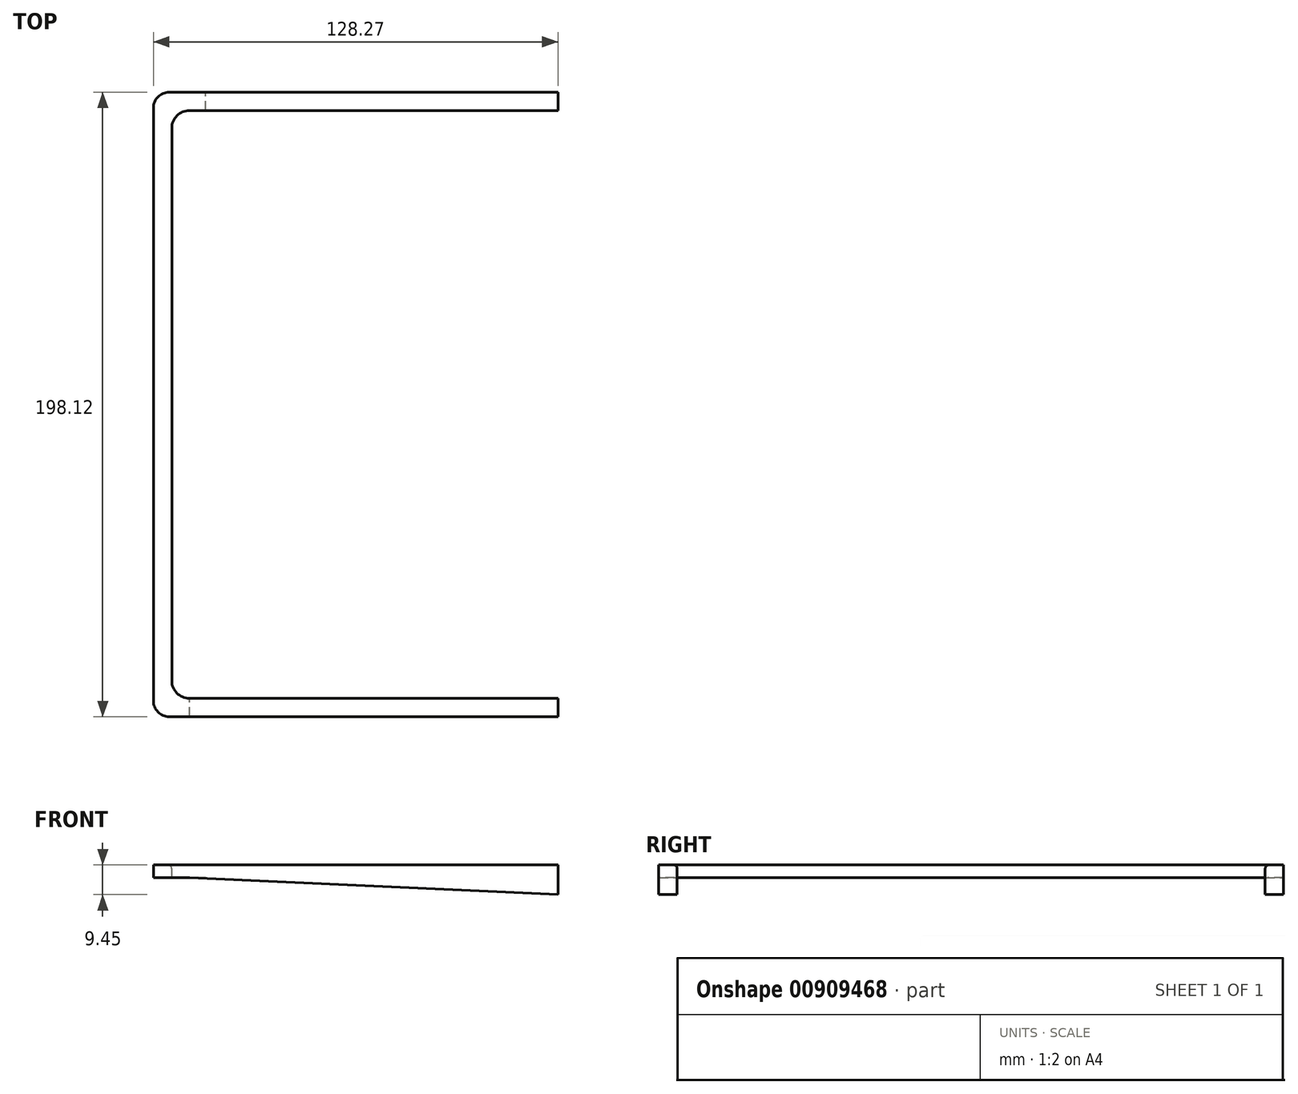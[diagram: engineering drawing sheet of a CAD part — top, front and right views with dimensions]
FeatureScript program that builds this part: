
annotation { "Feature Type Name" : "Feature", "Feature Type Description" : "" }
export const myFeature = defineFeature(function(context is Context, id is Id, definition is map)
    precondition{}
    {
        {
            var Q0;
            Q0=qCreatedBy(makeId("Top.planeOp"),FACE);
            var sketch = newSketch(context, id + "F0", { "sketchPlane" : qUnion([Q0])});
            skLineSegment(sketch, "E0", {"start": v(82.03, -99.06) * mm, "end": v(-41.16, -99.06) * mm});
            skArc(sketch, "E1", {"start": v(-46.24, -93.98) * mm, "mid": v(-44.75, -97.57) * mm, "end": v(-41.16, -99.06) * mm});
            skLineSegment(sketch, "E2", {"start": v(-46.24, -93.98) * mm, "end": v(-46.24, 93.98) * mm});
            skLineSegment(sketch, "E3", {"start": v(-41.16, 99.06) * mm, "end": v(82.03, 99.06) * mm});
            skArc(sketch, "E4", {"start": v(-41.16, 99.06) * mm, "mid": v(-44.75, 97.57) * mm, "end": v(-46.24, 93.98) * mm});
            skLineSegment(sketch, "E5", {"start": v(82.03, 93.22) * mm, "end": v(-34.8, 93.22) * mm});
            skArc(sketch, "E6", {"start": v(-34.8, 93.22) * mm, "mid": v(-38.76, 91.58) * mm, "end": v(-40.4, 87.63) * mm});
            skLineSegment(sketch, "E7", {"start": v(-40.4, 87.63) * mm, "end": v(-40.4, -87.63) * mm});
            skArc(sketch, "E8", {"start": v(-40.4, -87.63) * mm, "mid": v(-38.76, -91.58) * mm, "end": v(-34.8, -93.22) * mm});
            skLineSegment(sketch, "E9", {"start": v(-34.8, -93.22) * mm, "end": v(82.03, -93.22) * mm});
            skLineSegment(sketch, "E10", {"start": v(82.03, 99.06) * mm, "end": v(82.03, 93.22) * mm});
            skLineSegment(sketch, "E11", {"start": v(82.03, -93.22) * mm, "end": v(82.03, -99.06) * mm});
            skSolve(sketch);
        }
        {
            var Q0;
            Q0 = qSketchRegion(id + "F0", true);
            extrude(context, id + "F1", {"entities" : qUnion([Q0]), "oppositeDirection" : true, "depth" : 4.06 * mm, "offsetDistance" : 25.4 * mm});
        }
        {
            var Q0;
            Q0=makeQuery(id+"F1.opExtrude","CAP_FACE",FACE,{"disambiguationData":[OSD([sQuery(id+"F0.wireOp",EDGE,"E0"),sQuery(id+"F0.wireOp",EDGE,"E1"),sQuery(id+"F0.wireOp",EDGE,"E2"),sQuery(id+"F0.wireOp",EDGE,"E3"),sQuery(id+"F0.wireOp",EDGE,"E4"),sQuery(id+"F0.wireOp",EDGE,"E5"),sQuery(id+"F0.wireOp",EDGE,"E6"),sQuery(id+"F0.wireOp",EDGE,"E7"),sQuery(id+"F0.wireOp",EDGE,"E8"),sQuery(id+"F0.wireOp",EDGE,"E9"),sQuery(id+"F0.wireOp",EDGE,"E10"),sQuery(id+"F0.wireOp",EDGE,"E11")])],"isStart":true});
            var sketch = newSketch(context, id + "F2", { "sketchPlane" : qUnion([Q0])});
            skLineSegment(sketch, "E12", {"start": v(-34.8, 93.22) * mm, "end": v(-34.8, 99.06) * mm});
            skSolve(sketch);
        }
        {
            var Q0;
            Q0=makeQuery(id+"F1.opExtrude","SWEPT_FACE",FACE,{"disambiguationData":[OSD([sQuery(id+"F0.wireOp",EDGE,"E3")])]});
            var sketch = newSketch(context, id + "F3", { "sketchPlane" : qUnion([Q0])});
            skLineSegment(sketch, "E13", {"start": v(-82.03, 0) * mm, "end": v(-82.03, -9.45) * mm});
            skLineSegment(sketch, "E14", {"start": v(-82.03, -9.45) * mm, "end": v(35, -3.8) * mm});
            skLineSegment(sketch, "E15", {"start": v(35, -3.8) * mm, "end": v(34.8, 0) * mm});
            skSolve(sketch);
        }
        {
            var Q0;
            {var subQ0=sQuery(id+"F3.wireOp",EDGE,"E13");Q0=makeQuery(id+"F3.imprint","IMPRINT",FACE,{"disambiguationData":[TD([[makeQuery(id+"F3.imprint","IMPRINT",EDGE,{"derivedFrom":subQ0}),1.0]])]});}
            var Q1;
            Q1=makeQuery(id+"F1.opExtrude","SWEPT_FACE",FACE,{"disambiguationData":[OSD([sQuery(id+"F0.wireOp",EDGE,"E5")])]});
            extrude(context, id + "F4", {"entities" : qUnion([Q0]), "operationType" : NewBodyOperationType.ADD, "endBound" : BoundingType.UP_TO_SURFACE, "oppositeDirection" : true, "depth" : 25.4 * mm, "endBoundEntityFace" : qUnion([Q1]), "offsetDistance" : 25.4 * mm});
        }
        {
            var Q0;
            Q0=makeQuery(id+"F1.opExtrude","SWEPT_FACE",FACE,{"disambiguationData":[OSD([sQuery(id+"F0.wireOp",EDGE,"E9")])]});
            var sketch = newSketch(context, id + "F5", { "sketchPlane" : qUnion([Q0])});
            skLineSegment(sketch, "E16", {"start": v(-82.03, 0) * mm, "end": v(-82.03, -9.45) * mm});
            skLineSegment(sketch, "E17", {"start": v(-82.03, -9.45) * mm, "end": v(34.8, -4.06) * mm});
            skLineSegment(sketch, "E18", {"start": v(34.8, -4.06) * mm, "end": v(34.8, 0) * mm});
            skLineSegment(sketch, "E19", {"start": v(34.8, 0) * mm, "end": v(-82.03, 0) * mm});
            skSolve(sketch);
        }
        {
            var Q0;
            Q0 = qSketchRegion(id + "F5", true);
            extrude(context, id + "F6", {"entities" : qUnion([Q0]), "operationType" : NewBodyOperationType.ADD, "oppositeDirection" : true, "depth" : 5.84 * mm, "offsetDistance" : 25.4 * mm});
        }
        {
            var Q0;
            Q0=makeQuery(id+"F1.opExtrude","CAP_EDGE",EDGE,{"disambiguationData":[OSD([sQuery(id+"F0.wireOp",EDGE,"E5")])],"isStart":true});
            fillet(context, id + "F7", {"entities" : qUnion([Q0]), "radius" : 1.27 * mm, "tangentPropagation" : true, "allowEdgeOverflow" : false});
        }
    });
